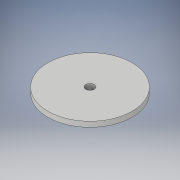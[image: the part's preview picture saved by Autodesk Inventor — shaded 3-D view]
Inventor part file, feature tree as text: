
AUTODESK INVENTOR PART (.ipt)
format: ipt  version: 2018 (Build 220112000, 112)  size: 95,232 bytes
history: native  units: in
note: dims shown in document units (in); Inventor stores cm internally (conversion verified against a paired STEP export)
features: extrude x1, sketch x1
ambient origin geometry x8: Origin, YZ Plane, XZ Plane, XY Plane, X Axis, Y Axis, Z Axis, Center Point
bodies: Solid1 (feature_tree)
feature tree (2):
  extrude  "Extrusion1"  Depth=0.125in
  sketch  "Sketch1"  dims[d0=2.0in d1=0.8985in d2=0.125in d3=0.0in]
